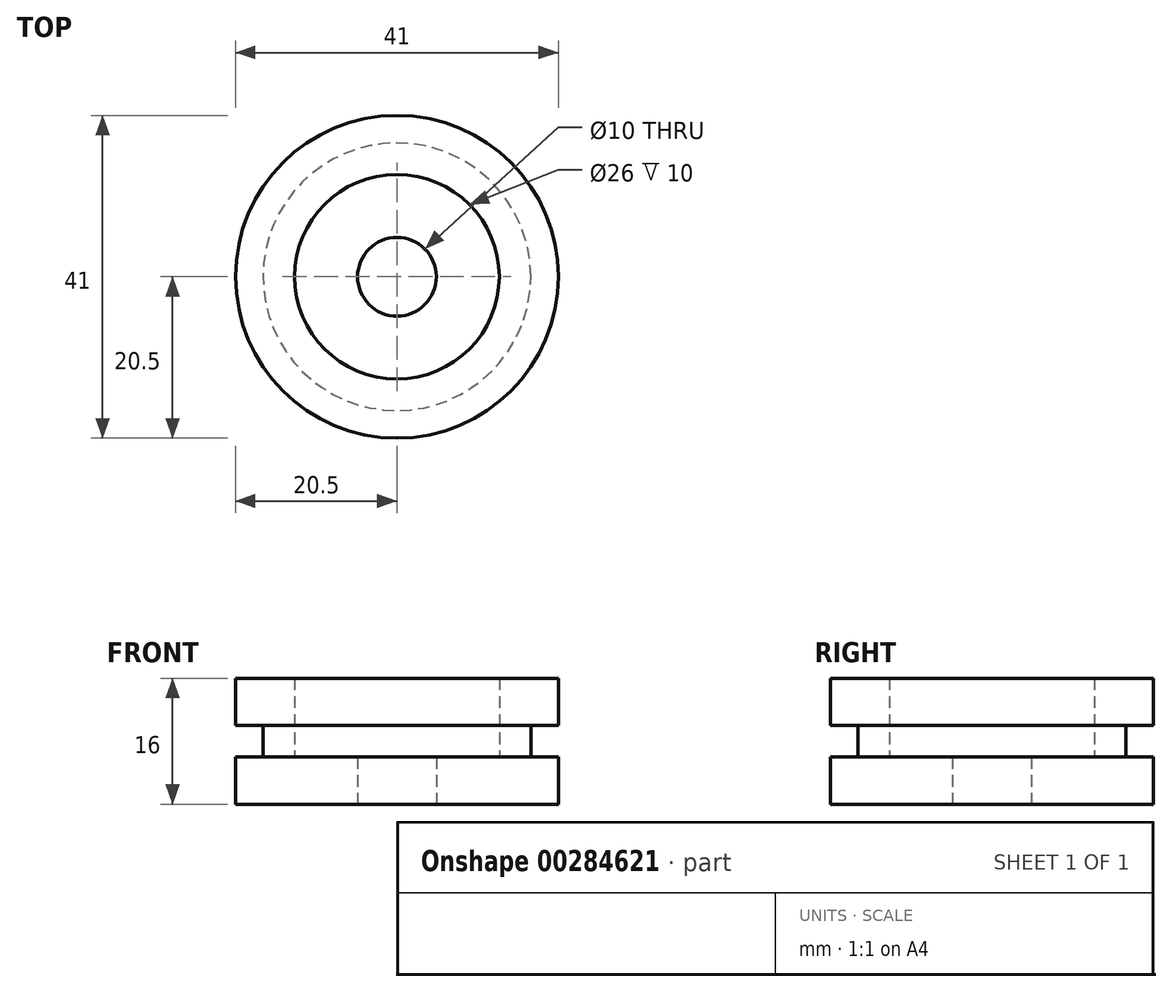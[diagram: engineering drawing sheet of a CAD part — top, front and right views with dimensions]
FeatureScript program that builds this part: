
annotation { "Feature Type Name" : "Feature", "Feature Type Description" : "" }
export const myFeature = defineFeature(function(context is Context, id is Id, definition is map)
    precondition{}
    {
        {
            var Q0;
            Q0=qCreatedBy(makeId("Front.planeOp"),FACE);
            var sketch = newSketch(context, id + "F0", { "sketchPlane" : qUnion([Q0])});
            skLineSegment(sketch, "E0", {"start": v(5, 0) * mm, "end": v(20.5, 0) * mm});
            skLineSegment(sketch, "E1", {"start": v(20.5, 0) * mm, "end": v(20.5, 6) * mm});
            skLineSegment(sketch, "E2", {"start": v(20.5, 6) * mm, "end": v(17, 6) * mm});
            skLineSegment(sketch, "E3", {"start": v(17, 6) * mm, "end": v(17, 10) * mm});
            skLineSegment(sketch, "E4", {"start": v(17, 10) * mm, "end": v(20.5, 10) * mm});
            skLineSegment(sketch, "E5", {"start": v(20.5, 10) * mm, "end": v(20.5, 16) * mm});
            skLineSegment(sketch, "E6", {"start": v(20.5, 16) * mm, "end": v(13, 16) * mm});
            skLineSegment(sketch, "E7", {"start": v(13, 16) * mm, "end": v(13, 6) * mm});
            skLineSegment(sketch, "E8", {"start": v(13, 6) * mm, "end": v(5, 6) * mm});
            skLineSegment(sketch, "E9", {"start": v(5, 6) * mm, "end": v(5, 0) * mm});
            skLineSegment(sketch, "E10", {"start": v(0, 0) * mm, "end": v(0, 18.35) * mm, "construction": true});
            skSolve(sketch);
        }
        {
            var Q0;
            Q0 = qSketchRegion(id + "F0", true);
            var Q1;
            Q1=sQuery(id+"F0.wireOp",EDGE,"E10");
            revolve(context, id + "F1", {"entities" : qUnion([Q0]), "axis" : qUnion([Q1]), "revolveType" : RevolveType.FULL});
        }
    });
